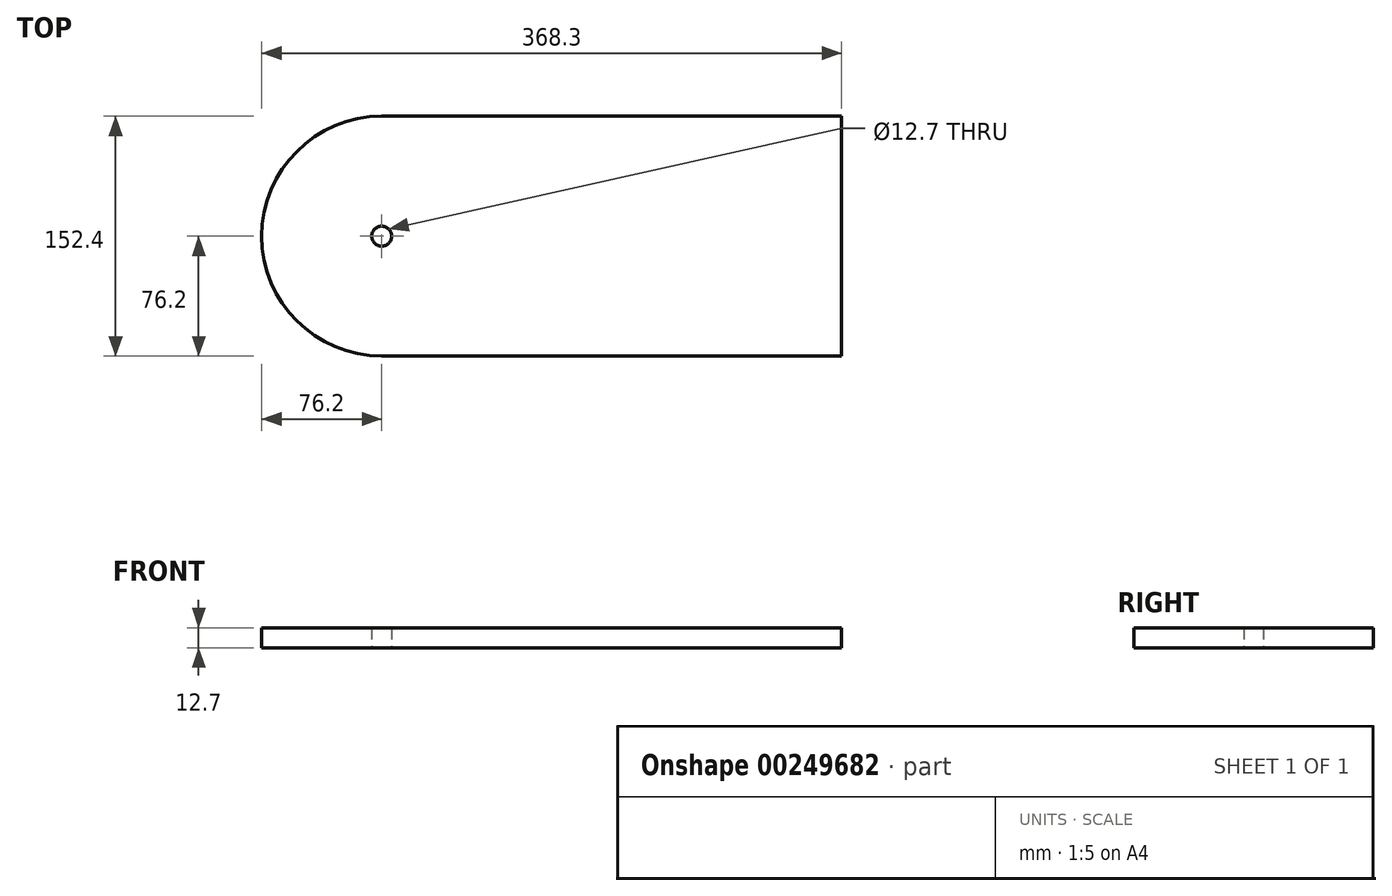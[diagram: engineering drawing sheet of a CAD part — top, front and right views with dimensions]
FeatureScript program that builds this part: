
annotation { "Feature Type Name" : "Feature", "Feature Type Description" : "" }
export const myFeature = defineFeature(function(context is Context, id is Id, definition is map)
    precondition{}
    {
        {
            var Q0;
            Q0=qCreatedBy(makeId("Top.planeOp"),FACE);
            var sketch = newSketch(context, id + "F0", { "sketchPlane" : qUnion([Q0])});
            skCircle(sketch, "E0", {"center": v(0, 0) * mm, "radius": 6.35 * mm});
            skArc(sketch, "E1", {"start": v(0, 76.2) * mm, "mid": v(-76.2, 0) * mm, "end": v(0, -76.2) * mm});
            skLineSegment(sketch, "E2", {"start": v(0, 76.2) * mm, "end": v(292.1, 76.2) * mm});
            skLineSegment(sketch, "E3", {"start": v(292.1, 76.2) * mm, "end": v(292.1, -76.2) * mm});
            skLineSegment(sketch, "E4", {"start": v(292.1, -76.2) * mm, "end": v(0, -76.2) * mm});
            skSolve(sketch);
        }
        {
            var Q0;
            Q0 = qSketchRegion(id + "F0", true);
            extrude(context, id + "F1", {"entities" : qUnion([Q0]), "depth" : 12.7 * mm});
        }
    });
